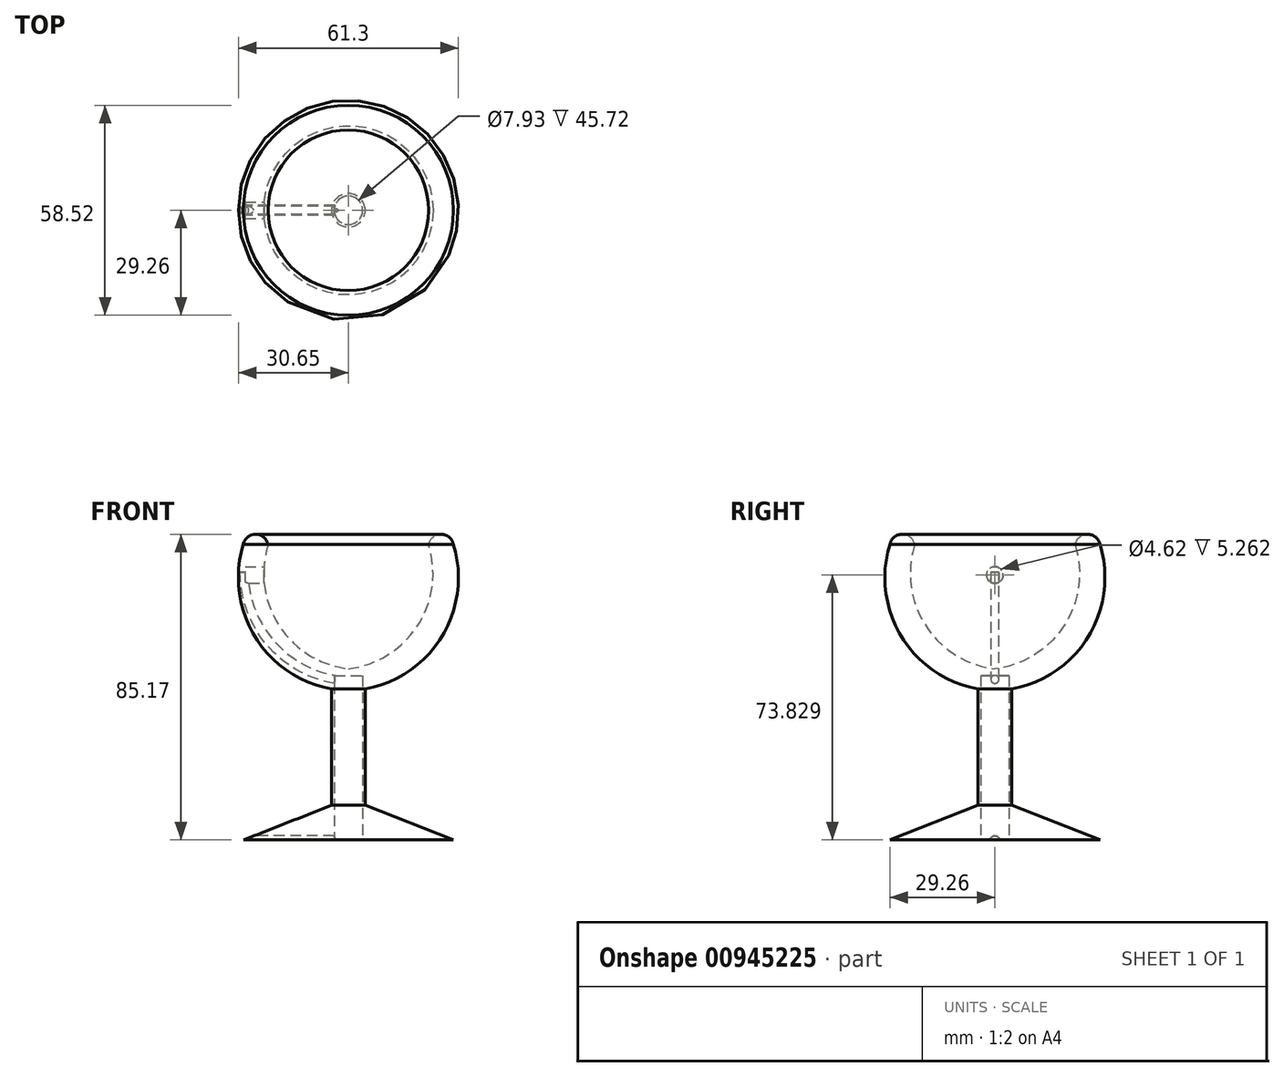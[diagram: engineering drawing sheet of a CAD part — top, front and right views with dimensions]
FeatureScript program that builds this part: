
annotation { "Feature Type Name" : "Feature", "Feature Type Description" : "" }
export const myFeature = defineFeature(function(context is Context, id is Id, definition is map)
    precondition{}
    {
        {
            var Q0;
            Q0=qCreatedBy(makeId("Front.planeOp"),FACE);
            var sketch = newSketch(context, id + "F0", { "sketchPlane" : qUnion([Q0])});
            skArc(sketch, "E0", {"start": v(0, 29.26) * mm, "mid": v(19.28, 41.26) * mm, "end": v(22.37, 63.75) * mm});
            skArc(sketch, "E1", {"start": v(4.68, 23.64) * mm, "mid": v(26.04, 38.27) * mm, "end": v(29.26, 63.95) * mm});
            skLineSegment(sketch, "E2", {"start": v(4.68, 23.64) * mm, "end": v(4.68, -8.77) * mm});
            skLineSegment(sketch, "E3", {"start": v(4.68, -8.77) * mm, "end": v(29.26, -18.43) * mm});
            skLineSegment(sketch, "E4", {"start": v(29.26, -18.43) * mm, "end": v(0, -18.43) * mm});
            skLineSegment(sketch, "E5", {"start": v(0, -18.43) * mm, "end": v(0, 29.26) * mm});
            skArc(sketch, "E6", {"start": v(29.26, 63.95) * mm, "mid": v(25.73, 66.74) * mm, "end": v(22.37, 63.75) * mm});
            skPoint(sketch, "E7.orphan", {"position": v(0, 23.16) * mm});
            skSolve(sketch);
        }
        {
            var Q0;
            Q0=makeQuery(id+"F0.imprint","IMPRINT",FACE,{"disambiguationData":[TD([[makeQuery(id+"F0.imprint","IMPRINT",EDGE,{"derivedFrom":sQuery(id+"F0.wireOp",EDGE,"E0")}),-1.0]])]});
            var Q1;
            Q1=sQuery(id+"F0.wireOp",EDGE,"E5");
            revolve(context, id + "F1", {"surfaceOperationType" : NewSurfaceOperationType.NEW, "entities" : qUnion([Q0]), "axis" : qUnion([Q1]), "revolveType" : RevolveType.FULL});
        }
        {
            var Q0;
            Q0=qCreatedBy(makeId("Front.planeOp"),FACE);
            var sketch = newSketch(context, id + "F2", { "sketchPlane" : qUnion([Q0])});
            skArc(sketch, "E8", {"start": v(-29.07, 56.05) * mm, "mid": v(-20.56, 35.16) * mm, "end": v(0, 25.9) * mm});
            skSolve(sketch);
        }
        {
            var Q0;
            Q0=qCreatedBy(makeId("Top.planeOp"),FACE);
            cPlane(context, id + "F3", {"entities" : qUnion([Q0]), "cplaneType" : CPlaneType.OFFSET, "offset" : 56.13 * mm, "width" : 152.4 * mm, "height" : 152.4 * mm});
        }
        {
            var Q0;
            Q0=qCreatedBy(id+"F3.planeOp",FACE);
            var sketch = newSketch(context, id + "F4", { "sketchPlane" : qUnion([Q0])});
            skCircle(sketch, "E9", {"center": v(-29.04, 0) * mm, "radius": 1.13 * mm});
            skSolve(sketch);
        }
        {
            var Q0;
            Q0 = qSketchRegion(id + "F4", true);
            var Q1;
            Q1 = qConstructionFilter(qBodyType(qCreatedBy(id + "F2" ,EDGE), BodyType.WIRE), ConstructionObject.NO);
            sweep(context, id + "F5", {"operationType" : NewBodyOperationType.REMOVE, "profiles" : qUnion([Q0]), "path" : qUnion([Q1])});
        }
        {
            var Q0;
            Q0=qCreatedBy(makeId("Right.planeOp"),FACE);
            cPlane(context, id + "F6", {"entities" : qUnion([Q0]), "cplaneType" : CPlaneType.OFFSET, "offset" : 19.8 * mm, "oppositeDirection" : true, "width" : 152.4 * mm, "height" : 152.4 * mm});
        }
        {
            var Q0;
            Q0=qCreatedBy(id+"F6.planeOp",FACE);
            var sketch = newSketch(context, id + "F7", { "sketchPlane" : qUnion([Q0])});
            skCircle(sketch, "E10", {"center": v(0, 55.4) * mm, "radius": 2.31 * mm});
            skSolve(sketch);
        }
        {
            var Q0;
            Q0=makeQuery(id+"F7.imprint","IMPRINT",FACE,{"disambiguationData":[TD([[makeQuery(id+"F7.imprint","IMPRINT",EDGE,{"derivedFrom":sQuery(id+"F7.wireOp",EDGE,"E10")}),1.0]])]});
            extrude(context, id + "F8", {"entities" : qUnion([Q0]), "operationType" : NewBodyOperationType.REMOVE, "oppositeDirection" : true, "depth" : 8.9 * mm, "offsetDistance" : 25.4 * mm});
        }
        {
            var Q0;
            Q0=makeQuery(id+"F1.opRevolve","SWEPT_FACE",FACE,{"disambiguationData":[OSD([sQuery(id+"F0.wireOp",EDGE,"E4")])]});
            var sketch = newSketch(context, id + "F9", { "sketchPlane" : qUnion([Q0])});
            skCircle(sketch, "E11", {"center": v(0, 0) * mm, "radius": 3.67 * mm});
            skSolve(sketch);
        }
        {
            var Q0;
            Q0=makeQuery(id+"F9.imprint","IMPRINT",FACE,{"disambiguationData":[TD([[makeQuery(id+"F9.imprint","IMPRINT",EDGE,{"derivedFrom":sQuery(id+"F9.wireOp",EDGE,"E11")}),1.0]])]});
            extrude(context, id + "F10", {"entities" : qUnion([Q0]), "operationType" : NewBodyOperationType.ADD, "oppositeDirection" : true, "depth" : 45.72 * mm, "offsetDistance" : 25.4 * mm});
        }
        {
            var Q0;
            Q0=makeQuery(id+"F1.opRevolve","SWEPT_FACE",FACE,{"disambiguationData":[OSD([sQuery(id+"F0.wireOp",EDGE,"E4")])]});
            var sketch = newSketch(context, id + "F11", { "sketchPlane" : qUnion([Q0])});
            skCircle(sketch, "E12", {"center": v(0, 0) * mm, "radius": 3.96 * mm});
            skSolve(sketch);
        }
        {
            var Q0;
            Q0=makeQuery(id+"F11.imprint","IMPRINT",FACE,{"disambiguationData":[TD([[makeQuery(id+"F11.imprint","IMPRINT",EDGE,{"derivedFrom":sQuery(id+"F11.wireOp",EDGE,"E12")}),1.0]])]});
            extrude(context, id + "F12", {"entities" : qUnion([Q0]), "operationType" : NewBodyOperationType.REMOVE, "oppositeDirection" : true, "depth" : 45.72 * mm, "offsetDistance" : 25.4 * mm});
        }
        {
            var Q0;
            Q0=qCreatedBy(id+"F6.planeOp",FACE);
            cPlane(context, id + "F13", {"entities" : qUnion([Q0]), "cplaneType" : CPlaneType.OFFSET, "offset" : 11.43 * mm, "oppositeDirection" : true, "width" : 152.4 * mm, "height" : 152.4 * mm});
        }
        {
            var Q0;
            Q0=qCreatedBy(id+"F13.planeOp",FACE);
            var sketch = newSketch(context, id + "F14", { "sketchPlane" : qUnion([Q0])});
            skCircle(sketch, "E13", {"center": v(0, -18.74) * mm, "radius": 1.44 * mm});
            skSolve(sketch);
        }
        {
            var Q0;
            Q0=makeQuery(id+"F14.imprint","IMPRINT",FACE,{"disambiguationData":[TD([[makeQuery(id+"F14.imprint","IMPRINT",EDGE,{"derivedFrom":sQuery(id+"F14.wireOp",EDGE,"E13")}),1.0]])]});
            extrude(context, id + "F15", {"entities" : qUnion([Q0]), "operationType" : NewBodyOperationType.REMOVE, "depth" : 33.27 * mm, "offsetDistance" : 25.4 * mm});
        }
    });
